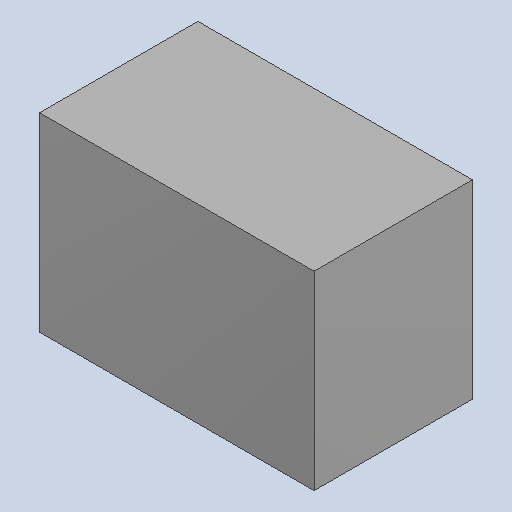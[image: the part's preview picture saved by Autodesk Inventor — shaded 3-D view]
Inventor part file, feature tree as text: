
AUTODESK INVENTOR PART (.ipt)
format: ipt  version: 2023.4 (Build 274418000, 418)  size: 82,432 bytes
history: native  units: mm
features: extrude x1
ambient origin geometry x8: Origin, YZ Plane, XZ Plane, XY Plane, X Axis, Y Axis, Z Axis, Center Point
bodies: Solid1 (feature_tree)
feature tree (1):
  extrude  "Extruded_2"  [1 undecoded]
note: 1 required parameter value undecoded (feature->parameter linkage not recoverable at this tier; creation-order binding heuristic only, values carry confidence <= 0.55)
